# Revit family: Bath-Freestanding-KOHLER-EVOK-K-99236T
name_source: partatom
category: Plumbing Fixtures
units: mm (PartAtom-declared; Revit-internal decimal feet)

## family parameters
Cut with Voids When Loaded = No
Host = Face
OmniClass Number = 23.31.15.00
OmniClass Title = Bathtubs
Part Type = Normal
Room Calculation Point = No
Round Connector Dimension = Use Diameter
Shared = No

## types (2) — shared parameters
ADA Compliant = No
Assembly Code = D2010500
CW Connection = No
Cold Water Inlet = Cold Water Inlet
Date Modified = 08/05/2023
Default Elevation = 0"
Drain Included = No
Finish = KOHLER-Acrylic-0-White
Flow Rate = 0 GPM
HW Connection = No
Height = 24 1/4"
Hot Water Inlet = Hot Water Inlet
Length = 66 15/16"
Manufacturer = Kohler Co.
Master Format 2014 = 22 41 19
Master Format 2014 Name = Residential Bathtubs
Material = Acrylic
Pressure = 0.00 psi
Product Name = Evok
URL = http://www.kohler.com.cn
Vent Connection = No
Waste Connection = Yes
Waste Water Outlet = Waste Water Outlet
WaterSense Certified = No
Width = 29 1/2"

## per-type parameters (varying)
| type | Description | Grab Bar | Model | Type |
| Without Grab Bar, 0-White | 1.7 M New Apron Oval Freestanding Bath Customized | No | K-99236T-0 | 1 |
| With Grab Bar, 0-White | 1.7 M Acrylic Freestanding Bath with Grab Bar | Yes | K-99236T-GR-0 | 2 |

## geometry (parser evidence)
native form markers: Sweep x5
no freeform markers — native parametric forms only
